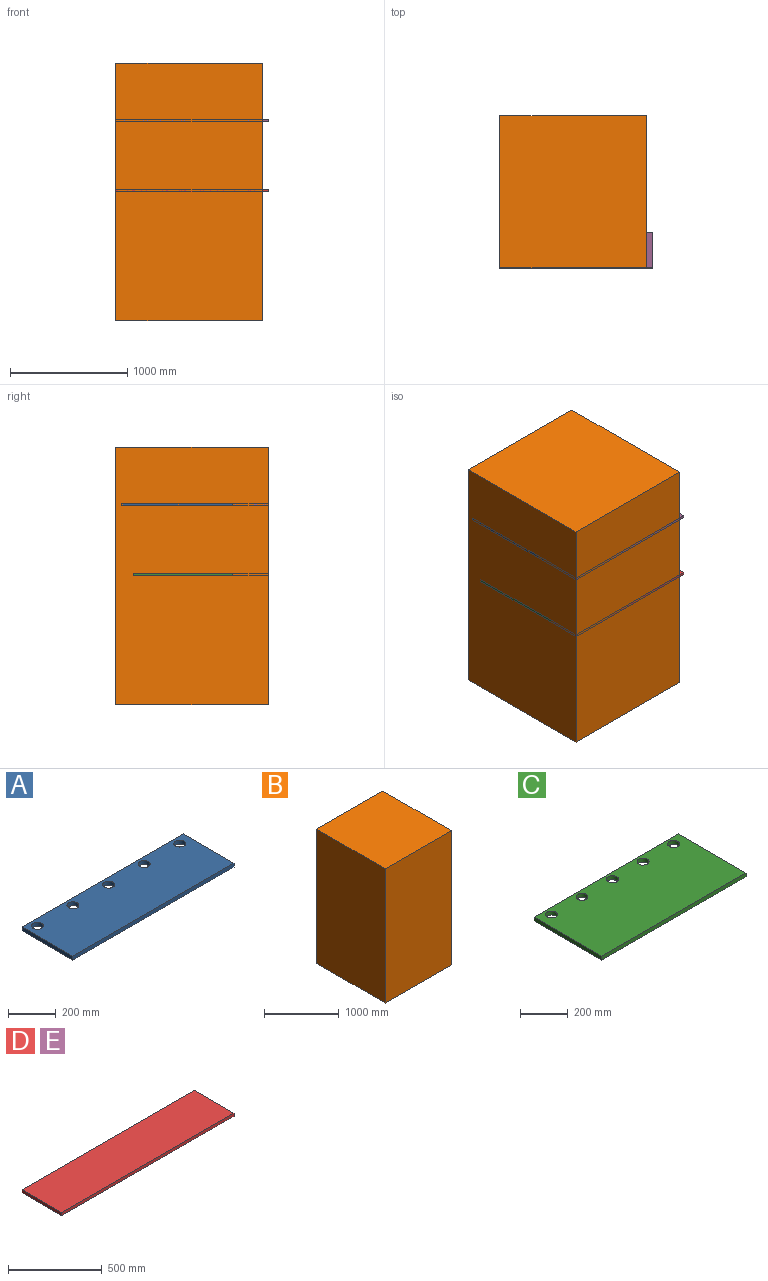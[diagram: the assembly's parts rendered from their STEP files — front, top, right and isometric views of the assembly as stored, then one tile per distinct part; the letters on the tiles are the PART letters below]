
ASSEMBLY  parts=5 mates=4
PART A: 11 faces, bbox 950x300x20 mm
  f0: plane 300x20mm, normal (-1,0,0), area 6000mm2, adj f1,f7,f9,f10
  f1: plane 950x20mm, normal (0,-1,0), area 19000mm2, adj f0,f2,f9,f10
  f2: plane 300x20mm, normal (1,0,0), area 6000mm2, adj f1,f7,f9,f10
  f3: cylinder r=25mm len=50mm, axis (0,0,-1), area 3141.6mm2, adj f9,f10
  f4: cylinder r=25mm len=50mm, axis (0,0,-1), area 3141.6mm2, adj f9,f10
  f5: cylinder r=25mm len=50mm, axis (0,0,-1), area 3141.6mm2, adj f9,f10
  f6: cylinder r=25mm len=50mm, axis (0,0,-1), area 3141.6mm2, adj f9,f10
  f7: plane 950x20mm, normal (0,1,0), area 19000mm2, adj f0,f2,f9,f10
  f8: cylinder r=25mm len=50mm, axis (0,0,-1), area 3141.6mm2, adj f9,f10
  f9: plane 950x300mm, normal (0,0,1), area 275182.5mm2, adj f0,f1,f2,f3,f4,f5,f6,f7
  f10: plane 950x300mm, normal (0,0,-1), area 275182.5mm2, adj f0,f1,f2,f3,f4,f5,f6,f7
PART B: 6 faces, bbox 1250x1300x2200 mm
  f0: plane 2200x1300mm, normal (1,0,0), area 2860000mm2, adj f1,f3,f4,f5
  f1: plane 2200x1250mm, normal (0,1,0), area 2750000mm2, adj f0,f2,f4,f5
  f2: plane 2200x1300mm, normal (-1,0,0), area 2860000mm2, adj f1,f3,f4,f5
  f3: plane 2200x1250mm, normal (0,-1,0), area 2750000mm2, adj f0,f2,f4,f5
  f4: plane 1300x1250mm, normal (0,0,1), area 1625000mm2, adj f0,f1,f2,f3
  f5: plane 1300x1250mm, normal (0,0,-1), area 1625000mm2, adj f0,f1,f2,f3
PART C: 11 faces, bbox 850x400x20 mm
  f0: plane 400x20mm, normal (-1,0,0), area 8000mm2, adj f1,f7,f9,f10
  f1: plane 850x20mm, normal (0,-1,0), area 17000mm2, adj f0,f2,f9,f10
  f2: plane 400x20mm, normal (1,0,0), area 8000mm2, adj f1,f7,f9,f10
  f3: cylinder r=25mm len=50mm, axis (0,0,-1), area 3141.6mm2, adj f9,f10
  f4: cylinder r=25mm len=50mm, axis (0,0,-1), area 3141.6mm2, adj f9,f10
  f5: cylinder r=25mm len=50mm, axis (0,0,-1), area 3141.6mm2, adj f9,f10
  f6: cylinder r=25mm len=50mm, axis (0,0,-1), area 3141.6mm2, adj f9,f10
  f7: plane 850x20mm, normal (0,1,0), area 17000mm2, adj f0,f2,f9,f10
  f8: cylinder r=25mm len=50mm, axis (0,0,-1), area 3141.6mm2, adj f9,f10
  f9: plane 850x400mm, normal (0,0,1), area 330182.5mm2, adj f0,f1,f2,f3,f4,f5,f6,f7
  f10: plane 850x400mm, normal (0,0,-1), area 330182.5mm2, adj f0,f1,f2,f3,f4,f5,f6,f7
PART D: 6 faces, bbox 1300x300x20 mm
  f0: plane 300x20mm, normal (-1,0,0), area 6000mm2, adj f1,f3,f4,f5
  f1: plane 1300x20mm, normal (0,-1,0), area 26000mm2, adj f0,f2,f4,f5
  f2: plane 300x20mm, normal (1,0,0), area 6000mm2, adj f1,f3,f4,f5
  f3: plane 1300x20mm, normal (0,1,0), area 26000mm2, adj f0,f2,f4,f5
  f4: plane 1300x300mm, normal (0,0,1), area 390000mm2, adj f0,f1,f2,f3
  f5: plane 1300x300mm, normal (0,0,-1), area 390000mm2, adj f0,f1,f2,f3
PART E: same geometry as D
PLACE A rot(axis=(0,0,1),90deg) t=(-1338.93,-1580.81,1178.13)mm
PLACE B t=(-1013.93,-1230.81,-520.87)mm
PLACE C rot(axis=(0,0,1),90deg) t=(-1238.93,-1580.81,583.13)mm
PLACE D t=(-1638.93,-1880.81,583.13)mm
PLACE E t=(-1638.93,-1880.81,1178.13)mm
MATE slider D.f4 <-> B.f5  axis (0,0,1) through (-1638.93,-1880.81,603.13)mm
MATE planar A.f9 <-> E.f4  axis (0,0,1) through (-1638.93,-1580.81,1198.13)mm
MATE slider E.f4 <-> B.f4  axis (0,0,1) through (-1638.93,-1880.81,1198.13)mm
MATE planar C.f9 <-> D.f4  axis (0,0,1) through (-1638.93,-1580.81,603.13)mm
